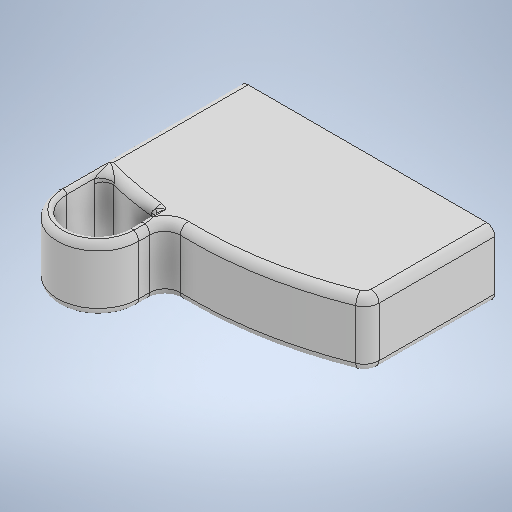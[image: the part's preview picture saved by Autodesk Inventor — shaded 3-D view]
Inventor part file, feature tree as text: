
AUTODESK INVENTOR PART (.ipt)
format: ipt  version: 2025.2 (Build 292293000, 293)  size: 434,688 bytes
history: native  units: in
note: dims shown in document units (in); Inventor stores cm internally (conversion verified against a paired STEP export)
features: fillet x6, other x1, extrude x1, sketch x1
ambient origin geometry x8: Origin, YZ Plane, XZ Plane, XY Plane, X Axis, Y Axis, Z Axis, Center Point
bodies: Body1 (feature_tree)
feature tree (9):
  other  "ソリッド1"
  extrude  "押し出し1"  Depth=3.3465in
  fillet  "フィレット4"  Radius=0.2756in
  fillet  "フィレット8"  Radius=9.8425in
  fillet  "フィレット9"  Radius=0.8661in
  fillet  "フィレット10"  Radius=0.3937in
  fillet  "フィレット11"  Radius=0.3937in
  fillet  "フィレット12"  Radius=0.8268in
  sketch  "スケッチ1"
